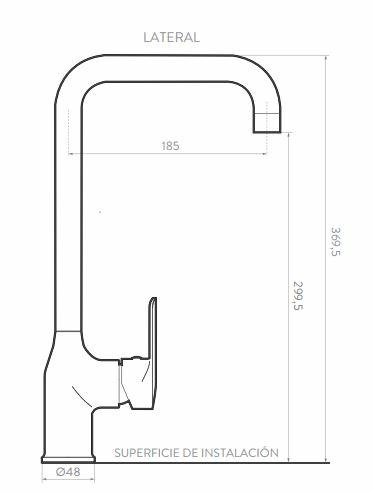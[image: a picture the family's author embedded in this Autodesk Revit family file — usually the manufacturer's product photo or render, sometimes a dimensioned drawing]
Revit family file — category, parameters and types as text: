
# Revit family: KR5025551_Grifería para Lavaplatos Monocontrol Koral Mate Black
name_source: partatom
category: Plumbing Fixtures
units: mm (PartAtom-declared; Revit-internal decimal feet)

## family parameters
Cut with Voids When Loaded = No
Host = Face
OmniClass Number = 23.31.11.00
OmniClass Title = Faucets
Part Type = Normal
Room Calculation Point = No
Round Connector Dimension = Use Diameter
Shared = No

## types (1)
- KR5025551_Grifería para Lavaplatos Monocontrol Koral Mate Black
    Alto = 370 mm
    Ancho = 48 mm  [stored 0.15748 ft]
    Capacidad de flujo = 60 psi: 7,28 L/min
    Creado por = IDD
    Default Elevation = 1219 mm
    Dimensiones generales producto (H * W * D) = 988 gr. - 2,17 lb
    Fabricante = Corona
    Fecha de creación = 09/10/2020
    Garantía = 30 años
    Material = Corona_Mate_Black
    Peso Neto aprox = 988 gr. - 2,17 lb
    Presion maxima = 125 psi (862 Kpa)
    Presion minima = 20 psi (138 Kpa)
    Profundidad = 221 mm
    Reference = KR5025551
    Temperatura de uso = 4ºC a 60ºC
    URL = https://corona.co

note: [stored X ft] marks values corroborated as IEEE doubles in the binary element streams (Revit-internal decimal feet)

## geometry (parser evidence)
native form markers: Sweep x3
no freeform markers — native parametric forms only
